# Revit family: Zumtobel RESCLITE PRO TRINOS
name_source: partatom
category: Lighting Fixtures
revit_build: Autodesk Revit 2016 (Build: 20150220_1215(x64)
units: mm (PartAtom-declared; Revit-internal decimal feet)

## family parameters
Always vertical = Yes
Cut with Voids When Loaded = No
Light Source = Yes
OmniClass Number = 23.80.70.11
OmniClass Title = Luminaries for Internal Lighting
Part Type = Normal
Room Calculation Point = No
Round Connector Dimension = Use Diameter
Shared = No
Work Plane-Based = No

## types (3) — shared parameters
Assembly Code = D5020200
Color Filter = 16777215
Description = Safety luminaire
Dimming Lamp Color Temperature Shift = <None>
Emit Shape Visible in Rendering = No
Emit from Rectangle Length = 85 mm  [stored 0.278871 ft]
Emit from Rectangle Width = 1000 mm  [stored 3.28084 ft]
Height = 62 mm  [stored 0.203412 ft]
Lamp = LED
Length = 1000 mm  [stored 3.28084 ft]
Manufacturer = Zumtobel Ligthing
Tilt Angle = 90.00°
URL = http://www.zumtobel.com
Voltage = 230
Width = 85 mm  [stored 0.278871 ft]

## per-type parameters (varying)
| type | Apparent Load | Model | Photometric Web File |
| RESCLITE PRO TRINOS ANT E3D WH | 5 VA | 42186056 | 42186056_(STD_LEO).IES |
| RESCLITE PRO TRINOS ESC HC | 7 VA | 42186066 | 42186066_(STD_LEO).IES |
| RESCLITE PRO TRINOS SPOT | 5 VA | 42186071 | 42186071_(STD_LEO).IES |

note: [stored X ft] marks values corroborated as IEEE doubles in the binary element streams (Revit-internal decimal feet)

## geometry (parser evidence)
native form markers: Sweep x3
no freeform markers — native parametric forms only
